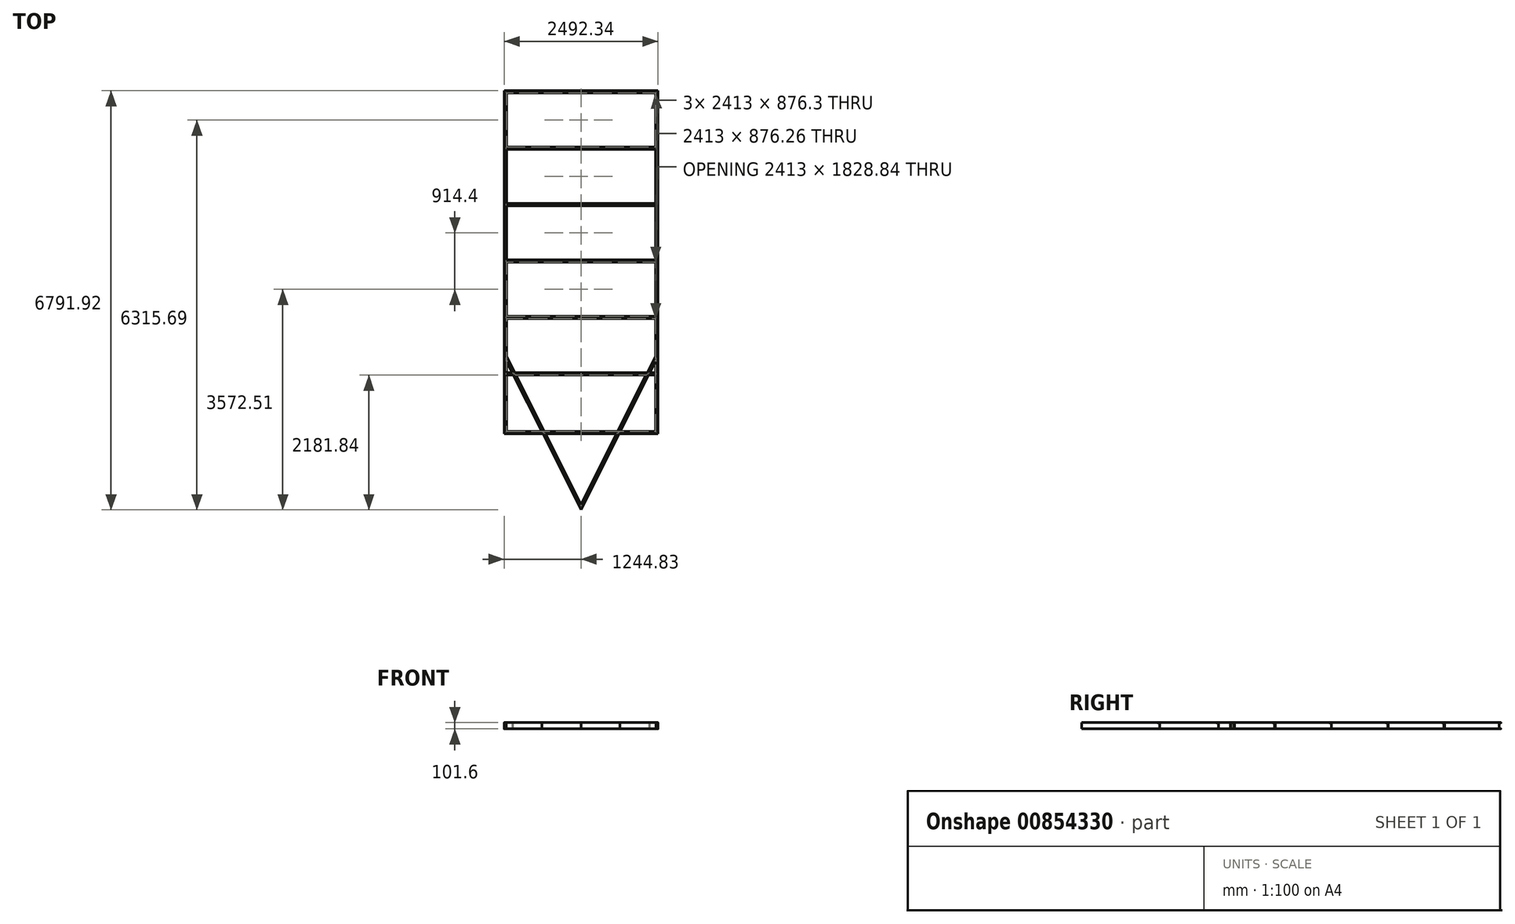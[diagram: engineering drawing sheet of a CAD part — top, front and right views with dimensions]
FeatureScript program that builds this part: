
annotation { "Feature Type Name" : "Feature", "Feature Type Description" : "" }
export const myFeature = defineFeature(function(context is Context, id is Id, definition is map)
    precondition{}
    {
        {
            var Q0;
            Q0=qCreatedBy(makeId("Top.planeOp"),FACE);
            var sketch = newSketch(context, id + "F0", { "sketchPlane" : qUnion([Q0])});
            skLineSegment(sketch, "E0.bottom", {"start": v(-1206.5, 0) * mm, "end": v(1206.5, 0) * mm});
            skLineSegment(sketch, "E0.top", {"start": v(-1206.5, 5486.4) * mm, "end": v(1206.5, 5486.4) * mm});
            skLineSegment(sketch, "E0.left", {"start": v(-1206.5, 0) * mm, "end": v(-1206.5, 5486.4) * mm});
            skLineSegment(sketch, "E0.right", {"start": v(1206.5, 0) * mm, "end": v(1206.5, 5486.4) * mm});
            skSolve(sketch);
        }
        {
            var Q0;
            Q0=qCreatedBy(makeId("Right.planeOp"),FACE);
            var sketch = newSketch(context, id + "F1", { "sketchPlane" : qUnion([Q0])});
            skLineSegment(sketch, "E1", {"start": v(0, 0) * mm, "end": v(0, 101.6) * mm});
            skLineSegment(sketch, "E2.MirrorCS", {"start": v(-38.1, 0) * mm, "end": v(0, 0) * mm});
            skLineSegment(sketch, "E3.MirrorCS", {"start": v(0, 101.6) * mm, "end": v(-38.1, 101.6) * mm});
            skLineSegment(sketch, "E4.MirrorCS", {"start": v(-38.1, 1.2) * mm, "end": v(-38.1, 0) * mm});
            skLineSegment(sketch, "E5.MirrorCS", {"start": v(-38.1, 101.6) * mm, "end": v(-38.1, 100.4) * mm});
            skArc(sketch, "E6.MirrorCS", {"start": v(-6.35, 9.65) * mm, "mid": v(-7.3, 7.25) * mm, "end": v(-9.65, 6.16) * mm});
            skArc(sketch, "E7.MirrorCS", {"start": v(-38.1, 1.2) * mm, "mid": v(-37.15, 3.6) * mm, "end": v(-34.8, 4.7) * mm});
            skArc(sketch, "E8.MirrorCS", {"start": v(-9.65, 95.44) * mm, "mid": v(-7.3, 94.35) * mm, "end": v(-6.35, 91.95) * mm});
            skArc(sketch, "E9.MirrorCS", {"start": v(-34.8, 96.9) * mm, "mid": v(-37.15, 98) * mm, "end": v(-38.1, 100.4) * mm});
            skLineSegment(sketch, "E10.MirrorCS", {"start": v(-6.35, 91.95) * mm, "end": v(-6.35, 9.65) * mm});
            skPoint(sketch, "E11.MirrorP", {"position": v(-6.35, 6.35) * mm});
            skLineSegment(sketch, "E12.MirrorCS", {"start": v(-34.8, 96.9) * mm, "end": v(-9.65, 95.44) * mm});
            skLineSegment(sketch, "E13.MirrorCS", {"start": v(-9.65, 6.16) * mm, "end": v(-34.8, 4.7) * mm});
            skPoint(sketch, "E14.MirrorP", {"position": v(-38.1, 97.1) * mm});
            skPoint(sketch, "E15.MirrorP", {"position": v(-38.1, 0) * mm});
            skPoint(sketch, "E16.MirrorP", {"position": v(-6.35, 95.25) * mm});
            skPoint(sketch, "E17.MirrorP", {"position": v(-38.1, 4.5) * mm});
            skSolve(sketch);
        }
        {
            var Q0;
            Q0 = qSketchRegion(id + "F1", true);
            var Q1;
            Q1 = qConstructionFilter(qBodyType(qCreatedBy(id + "F0" ,EDGE), BodyType.WIRE), ConstructionObject.NO);
            sweep(context, id + "F2", {"profiles" : qUnion([Q0]), "path" : qUnion([Q1])});
        }
        {
            var Q0;
            Q0=qCreatedBy(makeId("Top.planeOp"),FACE);
            var sketch = newSketch(context, id + "F3", { "sketchPlane" : qUnion([Q0])});
            skLineSegment(sketch, "E18", {"start": v(-1206.66, 1222.83) * mm, "end": v(0, -1181.1) * mm});
            skLineSegment(sketch, "E19", {"start": v(0, -1181.1) * mm, "end": v(1206.66, 1222.83) * mm});
            skLineSegment(sketch, "E20", {"start": v(-1335.09, 1222.83) * mm, "end": v(1347.67, 1222.83) * mm, "construction": true});
            skLineSegment(sketch, "E21", {"start": v(879.5, 1107.23) * mm, "end": v(1094.47, 999.32) * mm, "construction": true});
            skSolve(sketch);
        }
        {
            var Q0;
            Q0=sQuery(id+"F3.wireOp",VERTEX,"E19.end");
            var Q1;
            Q1=sQuery(id+"F3.wireOp",VERTEX,"E18.end");
            cPlane(context, id + "F4", {"entities" : qUnion([Q0, Q1]), "cplaneType" : CPlaneType.MID_PLANE, "offset" : 25 * mm, "width" : 150 * mm, "height" : 150 * mm});
        }
        {
            var Q0;
            Q0=qCreatedBy(id+"F4.planeOp",FACE);
            var sketch = newSketch(context, id + "F5", { "sketchPlane" : qUnion([Q0])});
            skLineSegment(sketch, "E22", {"start": v(568.58, 0) * mm, "end": v(568.58, 101.6) * mm});
            skLineSegment(sketch, "E23.MirrorCS", {"start": v(530.48, 0) * mm, "end": v(568.58, 0) * mm});
            skLineSegment(sketch, "E24.MirrorCS", {"start": v(568.58, 101.6) * mm, "end": v(530.48, 101.6) * mm});
            skLineSegment(sketch, "E25.MirrorCS", {"start": v(530.48, 1.2) * mm, "end": v(530.48, 0) * mm});
            skLineSegment(sketch, "E26.MirrorCS", {"start": v(530.48, 101.6) * mm, "end": v(530.48, 100.4) * mm});
            skArc(sketch, "E27.MirrorCS", {"start": v(562.23, 9.65) * mm, "mid": v(561.27, 7.25) * mm, "end": v(558.93, 6.16) * mm});
            skArc(sketch, "E28.MirrorCS", {"start": v(530.48, 1.2) * mm, "mid": v(531.43, 3.6) * mm, "end": v(533.78, 4.7) * mm});
            skArc(sketch, "E29.MirrorCS", {"start": v(558.93, 95.44) * mm, "mid": v(561.27, 94.35) * mm, "end": v(562.23, 91.95) * mm});
            skArc(sketch, "E30.MirrorCS", {"start": v(533.78, 96.9) * mm, "mid": v(531.43, 98) * mm, "end": v(530.48, 100.4) * mm});
            skLineSegment(sketch, "E31.MirrorCS", {"start": v(562.23, 91.95) * mm, "end": v(562.23, 9.65) * mm});
            skPoint(sketch, "E32.MirrorP", {"position": v(562.23, 6.35) * mm});
            skLineSegment(sketch, "E33.MirrorCS", {"start": v(533.78, 96.9) * mm, "end": v(558.93, 95.44) * mm});
            skLineSegment(sketch, "E34.MirrorCS", {"start": v(558.93, 6.16) * mm, "end": v(533.78, 4.7) * mm});
            skPoint(sketch, "E35.MirrorP", {"position": v(530.48, 97.1) * mm});
            skPoint(sketch, "E36.MirrorP", {"position": v(530.48, 0) * mm});
            skPoint(sketch, "E37.MirrorP", {"position": v(562.23, 95.25) * mm});
            skPoint(sketch, "E38.MirrorP", {"position": v(530.48, 4.5) * mm});
            skSolve(sketch);
        }
        {
            var Q0;
            Q0 = qSketchRegion(id + "F5", true);
            var Q1;
            Q1 = qConstructionFilter(qBodyType(qCreatedBy(id + "F3" ,EDGE), BodyType.WIRE), ConstructionObject.NO);
            sweep(context, id + "F6", {"operationType" : NewBodyOperationType.ADD, "profiles" : qUnion([Q0]), "path" : qUnion([Q1])});
        }
        {
            var Q0;
            Q0=qCreatedBy(makeId("Top.planeOp"),FACE);
            var sketch = newSketch(context, id + "F7", { "sketchPlane" : qUnion([Q0])});
            skLineSegment(sketch, "E39.0", {"start": v(-1244.83, 952.5) * mm, "end": v(1247.51, 952.5) * mm});
            skSolve(sketch);
        }
        {
            var Q0;
            Q0=qCreatedBy(makeId("Right.planeOp"),FACE);
            var sketch = newSketch(context, id + "F8", { "sketchPlane" : qUnion([Q0])});
            skLineSegment(sketch, "E40", {"start": v(952.54, 0) * mm, "end": v(952.54, 101.6) * mm});
            skLineSegment(sketch, "E41.MirrorCS", {"start": v(914.44, 0) * mm, "end": v(952.54, 0) * mm});
            skLineSegment(sketch, "E42.MirrorCS", {"start": v(952.54, 101.6) * mm, "end": v(914.44, 101.6) * mm});
            skLineSegment(sketch, "E43.MirrorCS", {"start": v(914.44, 1.2) * mm, "end": v(914.44, 0) * mm});
            skLineSegment(sketch, "E44.MirrorCS", {"start": v(914.44, 101.6) * mm, "end": v(914.44, 100.4) * mm});
            skArc(sketch, "E45.MirrorCS", {"start": v(946.19, 9.65) * mm, "mid": v(945.23, 7.25) * mm, "end": v(942.89, 6.16) * mm});
            skArc(sketch, "E46.MirrorCS", {"start": v(914.44, 1.2) * mm, "mid": v(915.4, 3.6) * mm, "end": v(917.73, 4.7) * mm});
            skArc(sketch, "E47.MirrorCS", {"start": v(942.89, 95.44) * mm, "mid": v(945.23, 94.35) * mm, "end": v(946.19, 91.95) * mm});
            skArc(sketch, "E48.MirrorCS", {"start": v(917.73, 96.9) * mm, "mid": v(915.4, 98) * mm, "end": v(914.44, 100.4) * mm});
            skLineSegment(sketch, "E49.MirrorCS", {"start": v(946.19, 91.95) * mm, "end": v(946.19, 9.65) * mm});
            skPoint(sketch, "E50.MirrorP", {"position": v(946.19, 6.35) * mm});
            skLineSegment(sketch, "E51.MirrorCS", {"start": v(917.73, 96.9) * mm, "end": v(942.89, 95.44) * mm});
            skLineSegment(sketch, "E52.MirrorCS", {"start": v(942.89, 6.16) * mm, "end": v(917.73, 4.7) * mm});
            skPoint(sketch, "E53.MirrorP", {"position": v(914.44, 97.1) * mm});
            skPoint(sketch, "E54.MirrorP", {"position": v(914.44, 0) * mm});
            skPoint(sketch, "E55.MirrorP", {"position": v(946.19, 95.25) * mm});
            skPoint(sketch, "E56.MirrorP", {"position": v(914.44, 4.5) * mm});
            skPoint(sketch, "E57.1.0.0", {"position": v(1860.59, 6.35) * mm});
            skPoint(sketch, "E57.1.0.1", {"position": v(1828.84, 97.1) * mm});
            skPoint(sketch, "E57.1.0.2", {"position": v(1828.84, 4.5) * mm});
            skLineSegment(sketch, "E57.1.0.3", {"start": v(1866.94, 0) * mm, "end": v(1866.94, 101.6) * mm});
            skPoint(sketch, "E57.1.0.4", {"position": v(1828.84, 0) * mm});
            skPoint(sketch, "E57.1.0.5", {"position": v(1860.59, 95.25) * mm});
            skLineSegment(sketch, "E57.1.0.6", {"start": v(1860.59, 91.95) * mm, "end": v(1860.59, 9.65) * mm});
            skLineSegment(sketch, "E57.1.0.7", {"start": v(1828.84, 0) * mm, "end": v(1866.94, 0) * mm});
            skLineSegment(sketch, "E57.1.0.8", {"start": v(1866.94, 101.6) * mm, "end": v(1828.84, 101.6) * mm});
            skLineSegment(sketch, "E57.1.0.9", {"start": v(1857.29, 6.16) * mm, "end": v(1832.13, 4.7) * mm});
            skLineSegment(sketch, "E57.1.0.10", {"start": v(1832.13, 96.9) * mm, "end": v(1857.29, 95.44) * mm});
            skArc(sketch, "E57.1.0.11", {"start": v(1860.59, 9.65) * mm, "mid": v(1859.63, 7.25) * mm, "end": v(1857.29, 6.16) * mm});
            skArc(sketch, "E57.1.0.12", {"start": v(1857.29, 95.44) * mm, "mid": v(1859.63, 94.35) * mm, "end": v(1860.59, 91.95) * mm});
            skArc(sketch, "E57.1.0.13", {"start": v(1832.13, 96.9) * mm, "mid": v(1829.8, 98) * mm, "end": v(1828.84, 100.4) * mm});
            skArc(sketch, "E57.1.0.14", {"start": v(1828.84, 1.2) * mm, "mid": v(1829.8, 3.6) * mm, "end": v(1832.13, 4.7) * mm});
            skLineSegment(sketch, "E57.1.0.15", {"start": v(1828.84, 1.2) * mm, "end": v(1828.84, 0) * mm});
            skLineSegment(sketch, "E57.1.0.16", {"start": v(1828.84, 101.6) * mm, "end": v(1828.84, 100.4) * mm});
            skPoint(sketch, "E57.2.0.0", {"position": v(2774.99, 6.35) * mm});
            skPoint(sketch, "E57.2.0.1", {"position": v(2743.24, 97.1) * mm});
            skPoint(sketch, "E57.2.0.2", {"position": v(2743.24, 4.5) * mm});
            skLineSegment(sketch, "E57.2.0.3", {"start": v(2781.34, 0) * mm, "end": v(2781.34, 101.6) * mm});
            skPoint(sketch, "E57.2.0.4", {"position": v(2743.24, 0) * mm});
            skPoint(sketch, "E57.2.0.5", {"position": v(2774.99, 95.25) * mm});
            skLineSegment(sketch, "E57.2.0.6", {"start": v(2774.99, 91.95) * mm, "end": v(2774.99, 9.65) * mm});
            skLineSegment(sketch, "E57.2.0.7", {"start": v(2743.24, 0) * mm, "end": v(2781.34, 0) * mm});
            skLineSegment(sketch, "E57.2.0.8", {"start": v(2781.34, 101.6) * mm, "end": v(2743.24, 101.6) * mm});
            skLineSegment(sketch, "E57.2.0.9", {"start": v(2771.69, 6.16) * mm, "end": v(2746.53, 4.7) * mm});
            skLineSegment(sketch, "E57.2.0.10", {"start": v(2746.53, 96.9) * mm, "end": v(2771.69, 95.44) * mm});
            skArc(sketch, "E57.2.0.11", {"start": v(2774.99, 9.65) * mm, "mid": v(2774.03, 7.25) * mm, "end": v(2771.69, 6.16) * mm});
            skArc(sketch, "E57.2.0.12", {"start": v(2771.69, 95.44) * mm, "mid": v(2774.03, 94.35) * mm, "end": v(2774.99, 91.95) * mm});
            skArc(sketch, "E57.2.0.13", {"start": v(2746.53, 96.9) * mm, "mid": v(2744.2, 98) * mm, "end": v(2743.24, 100.4) * mm});
            skArc(sketch, "E57.2.0.14", {"start": v(2743.24, 1.2) * mm, "mid": v(2744.2, 3.6) * mm, "end": v(2746.53, 4.7) * mm});
            skLineSegment(sketch, "E57.2.0.15", {"start": v(2743.24, 1.2) * mm, "end": v(2743.24, 0) * mm});
            skLineSegment(sketch, "E57.2.0.16", {"start": v(2743.24, 101.6) * mm, "end": v(2743.24, 100.4) * mm});
            skPoint(sketch, "E57.3.0.0", {"position": v(3689.39, 6.35) * mm});
            skPoint(sketch, "E57.3.0.1", {"position": v(3657.64, 97.1) * mm});
            skPoint(sketch, "E57.3.0.2", {"position": v(3657.64, 4.5) * mm});
            skLineSegment(sketch, "E57.3.0.3", {"start": v(3695.74, 0) * mm, "end": v(3695.74, 101.6) * mm});
            skPoint(sketch, "E57.3.0.4", {"position": v(3657.64, 0) * mm});
            skPoint(sketch, "E57.3.0.5", {"position": v(3689.39, 95.25) * mm});
            skLineSegment(sketch, "E57.3.0.6", {"start": v(3689.39, 91.95) * mm, "end": v(3689.39, 9.65) * mm});
            skLineSegment(sketch, "E57.3.0.7", {"start": v(3657.64, 0) * mm, "end": v(3695.74, 0) * mm});
            skLineSegment(sketch, "E57.3.0.8", {"start": v(3695.74, 101.6) * mm, "end": v(3657.64, 101.6) * mm});
            skLineSegment(sketch, "E57.3.0.9", {"start": v(3686.09, 6.16) * mm, "end": v(3660.93, 4.7) * mm});
            skLineSegment(sketch, "E57.3.0.10", {"start": v(3660.93, 96.9) * mm, "end": v(3686.09, 95.44) * mm});
            skArc(sketch, "E57.3.0.11", {"start": v(3689.39, 9.65) * mm, "mid": v(3688.43, 7.25) * mm, "end": v(3686.09, 6.16) * mm});
            skArc(sketch, "E57.3.0.12", {"start": v(3686.09, 95.44) * mm, "mid": v(3688.43, 94.35) * mm, "end": v(3689.39, 91.95) * mm});
            skArc(sketch, "E57.3.0.13", {"start": v(3660.93, 96.9) * mm, "mid": v(3658.6, 98) * mm, "end": v(3657.64, 100.4) * mm});
            skArc(sketch, "E57.3.0.14", {"start": v(3657.64, 1.2) * mm, "mid": v(3658.6, 3.6) * mm, "end": v(3660.93, 4.7) * mm});
            skLineSegment(sketch, "E57.3.0.15", {"start": v(3657.64, 1.2) * mm, "end": v(3657.64, 0) * mm});
            skLineSegment(sketch, "E57.3.0.16", {"start": v(3657.64, 101.6) * mm, "end": v(3657.64, 100.4) * mm});
            skPoint(sketch, "E57.4.0.0", {"position": v(4603.79, 6.35) * mm});
            skPoint(sketch, "E57.4.0.1", {"position": v(4572.04, 97.1) * mm});
            skPoint(sketch, "E57.4.0.2", {"position": v(4572.04, 4.5) * mm});
            skLineSegment(sketch, "E57.4.0.3", {"start": v(4610.14, 0) * mm, "end": v(4610.14, 101.6) * mm});
            skPoint(sketch, "E57.4.0.4", {"position": v(4572.04, 0) * mm});
            skPoint(sketch, "E57.4.0.5", {"position": v(4603.79, 95.25) * mm});
            skLineSegment(sketch, "E57.4.0.6", {"start": v(4603.79, 91.95) * mm, "end": v(4603.79, 9.65) * mm});
            skLineSegment(sketch, "E57.4.0.7", {"start": v(4572.04, 0) * mm, "end": v(4610.14, 0) * mm});
            skLineSegment(sketch, "E57.4.0.8", {"start": v(4610.14, 101.6) * mm, "end": v(4572.04, 101.6) * mm});
            skLineSegment(sketch, "E57.4.0.9", {"start": v(4600.49, 6.16) * mm, "end": v(4575.33, 4.7) * mm});
            skLineSegment(sketch, "E57.4.0.10", {"start": v(4575.33, 96.9) * mm, "end": v(4600.49, 95.44) * mm});
            skArc(sketch, "E57.4.0.11", {"start": v(4603.79, 9.65) * mm, "mid": v(4602.83, 7.25) * mm, "end": v(4600.49, 6.16) * mm});
            skArc(sketch, "E57.4.0.12", {"start": v(4600.49, 95.44) * mm, "mid": v(4602.83, 94.35) * mm, "end": v(4603.79, 91.95) * mm});
            skArc(sketch, "E57.4.0.13", {"start": v(4575.33, 96.9) * mm, "mid": v(4573, 98) * mm, "end": v(4572.04, 100.4) * mm});
            skArc(sketch, "E57.4.0.14", {"start": v(4572.04, 1.2) * mm, "mid": v(4573, 3.6) * mm, "end": v(4575.33, 4.7) * mm});
            skLineSegment(sketch, "E57.4.0.15", {"start": v(4572.04, 1.2) * mm, "end": v(4572.04, 0) * mm});
            skLineSegment(sketch, "E57.4.0.16", {"start": v(4572.04, 101.6) * mm, "end": v(4572.04, 100.4) * mm});
            skLineSegment(sketch, "E57.direction1", {"start": v(914.44, 0) * mm, "end": v(1828.84, 0) * mm, "construction": true});
            skSolve(sketch);
        }
        {
            var Q0;
            Q0 = qSketchRegion(id + "F8", true);
            var Q1;
            Q1 = qConstructionFilter(qBodyType(qCreatedBy(id + "F7" ,EDGE), BodyType.WIRE), ConstructionObject.NO);
            sweep(context, id + "F9", {"operationType" : NewBodyOperationType.ADD, "profiles" : qUnion([Q0]), "path" : qUnion([Q1])});
        }
    });
